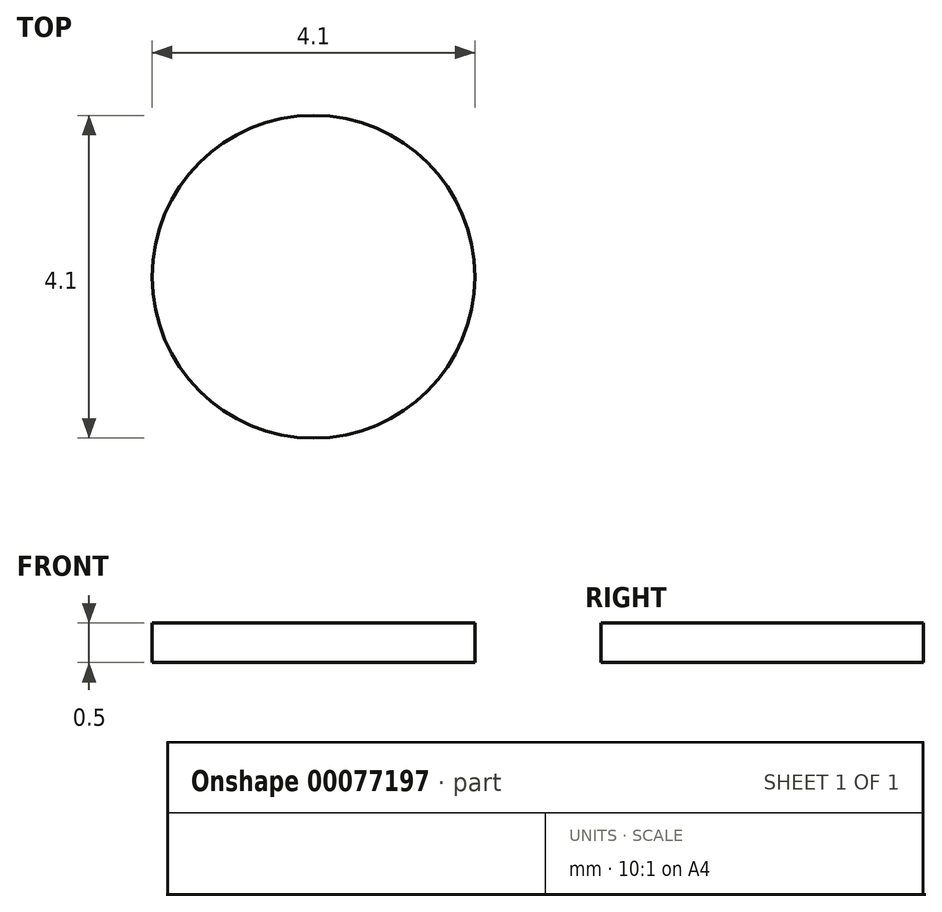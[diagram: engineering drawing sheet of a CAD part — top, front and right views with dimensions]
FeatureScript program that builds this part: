
annotation { "Feature Type Name" : "Feature", "Feature Type Description" : "" }
export const myFeature = defineFeature(function(context is Context, id is Id, definition is map)
    precondition{}
    {
        {
            var Q0;
            Q0=qCreatedBy(makeId("Top.planeOp"),FACE);
            var sketch = newSketch(context, id + "F0", { "sketchPlane" : qUnion([Q0])});
            skCircle(sketch, "E0", {"center": v(0, 0) * mm, "radius": 2.05 * mm});
            skSolve(sketch);
        }
        {
            var Q0;
            Q0=qSketchRegion(id+"F0",true);
            extrude(context, id + "F1", {"entities" : qUnion([Q0]), "depth" : .5 * mm});
        }
    });
